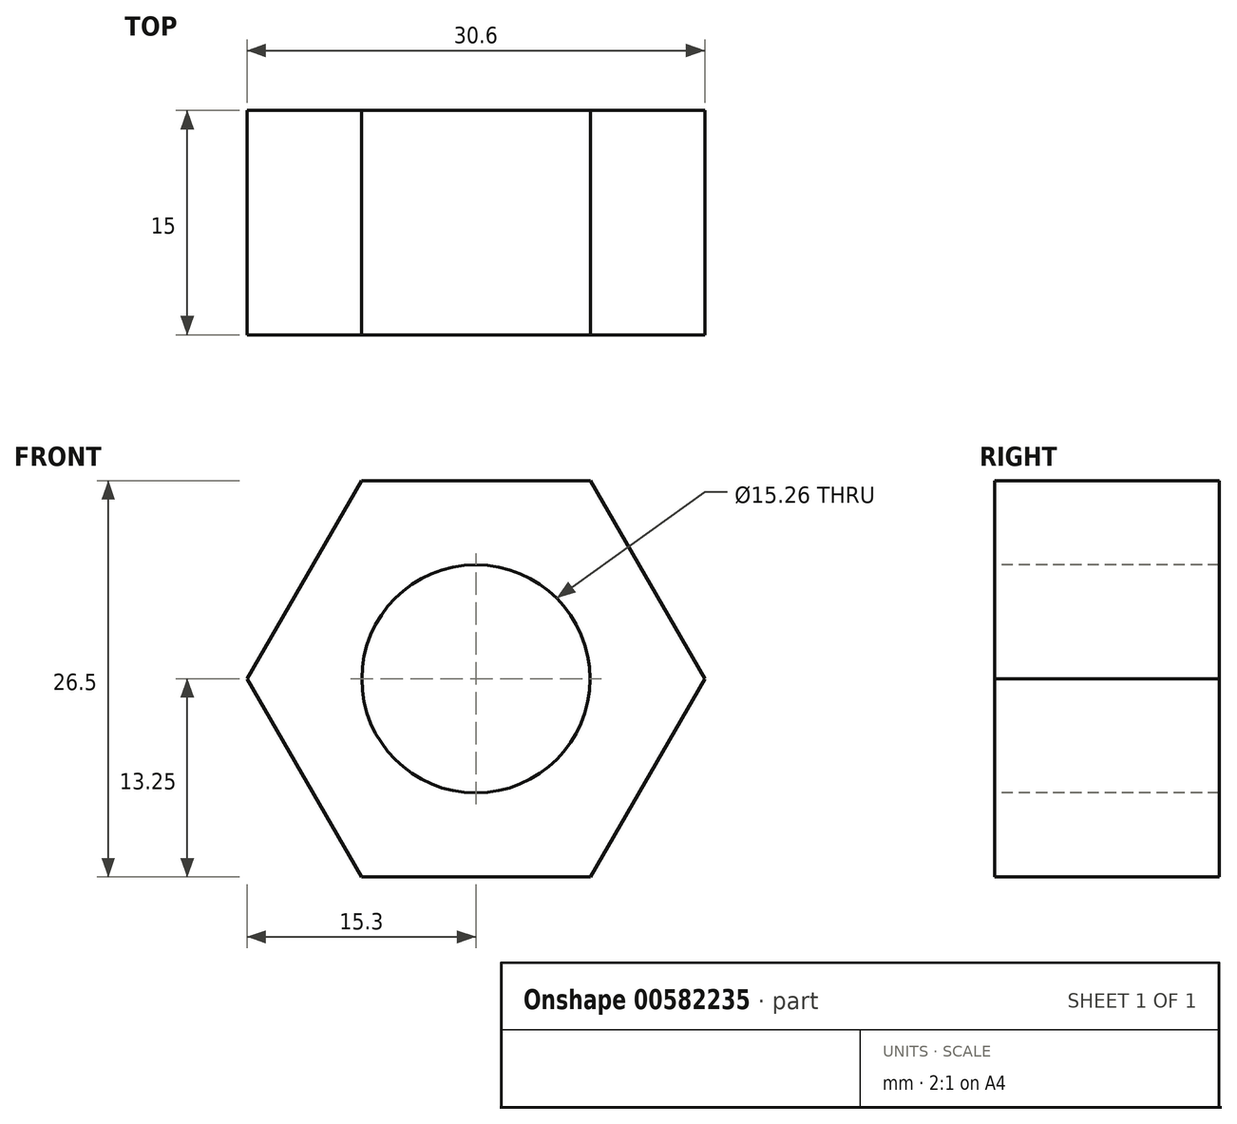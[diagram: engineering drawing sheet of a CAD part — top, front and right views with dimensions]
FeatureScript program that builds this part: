
annotation { "Feature Type Name" : "Feature", "Feature Type Description" : "" }
export const myFeature = defineFeature(function(context is Context, id is Id, definition is map)
    precondition{}
    {
        {
            var Q0;
            Q0=qCreatedBy(makeId("Front.planeOp"),FACE);
            var sketch = newSketch(context, id + "F0", { "sketchPlane" : qUnion([Q0])});
            skCircle(sketch, "E0.cCircle", {"center": v(0, 0) * mm, "radius": 13.25 * mm, "construction": true});
            skLineSegment(sketch, "E0.0", {"start": v(-7.65, 13.25) * mm, "end": v(7.65, 13.25) * mm});
            skLineSegment(sketch, "E0.1", {"start": v(7.65, 13.25) * mm, "end": v(15.3, 0) * mm});
            skLineSegment(sketch, "E0.2", {"start": v(15.3, 0) * mm, "end": v(7.65, -13.25) * mm});
            skLineSegment(sketch, "E0.3", {"start": v(7.65, -13.25) * mm, "end": v(-7.65, -13.25) * mm});
            skLineSegment(sketch, "E0.4", {"start": v(-7.65, -13.25) * mm, "end": v(-15.3, 0) * mm});
            skLineSegment(sketch, "E0.5", {"start": v(-15.3, 0) * mm, "end": v(-7.65, 13.25) * mm});
            skPoint(sketch, "E0.0.midPoint", {"position": v(0, 13.25) * mm});
            skSolve(sketch);
        }
        {
            var Q0;
            Q0 = qSketchRegion(id + "F0", true);
            extrude(context, id + "F1", {"entities" : qUnion([Q0]), "depth" : 15 * mm, "offsetDistance" : 25 * mm});
        }
        {
            var Q0;
            Q0=makeQuery(id+"F1.opExtrude","CAP_FACE",FACE,{"disambiguationData":[OSD([sQuery(id+"F0.wireOp",EDGE,"E0.0"),sQuery(id+"F0.wireOp",EDGE,"E0.1"),sQuery(id+"F0.wireOp",EDGE,"E0.2"),sQuery(id+"F0.wireOp",EDGE,"E0.3"),sQuery(id+"F0.wireOp",EDGE,"E0.4"),sQuery(id+"F0.wireOp",EDGE,"E0.5")])],"isStart":false});
            var sketch = newSketch(context, id + "F2", { "sketchPlane" : qUnion([Q0])});
            skCircle(sketch, "E1", {"center": v(0, 0) * mm, "radius": 7.63 * mm});
            skSolve(sketch);
        }
        {
            var Q0;
            Q0=makeQuery(id+"F2.imprint","IMPRINT",FACE,{"disambiguationData":[TD([[makeQuery(id+"F2.imprint","IMPRINT",EDGE,{"derivedFrom":sQuery(id+"F2.wireOp",EDGE,"E1")}),1.0]])]});
            extrude(context, id + "F3", {"entities" : qUnion([Q0]), "operationType" : NewBodyOperationType.REMOVE, "endBound" : BoundingType.THROUGH_ALL, "oppositeDirection" : true, "depth" : 25 * mm, "offsetDistance" : 25 * mm});
        }
    });
